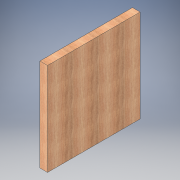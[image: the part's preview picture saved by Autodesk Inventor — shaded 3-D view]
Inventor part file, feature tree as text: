
AUTODESK INVENTOR PART (.ipt)
format: ipt  version: 2017 (Build 210142000, 142)  size: 114,688 bytes
history: native  units: in
note: dims shown in document units (in); Inventor stores cm internally (conversion verified against a paired STEP export)
features: extrude x1, sketch x1
ambient origin geometry x8: Origin, YZ Plane, XZ Plane, XY Plane, X Axis, Y Axis, Z Axis, Center Point
bodies: Solid1 (feature_tree)
feature tree (2):
  extrude  "Extrusion1"  Depth=36.0in
  sketch  "Sketch1"  dims[d0=3.0in d1=36.0in d2=36.0in d3=0.0in]
